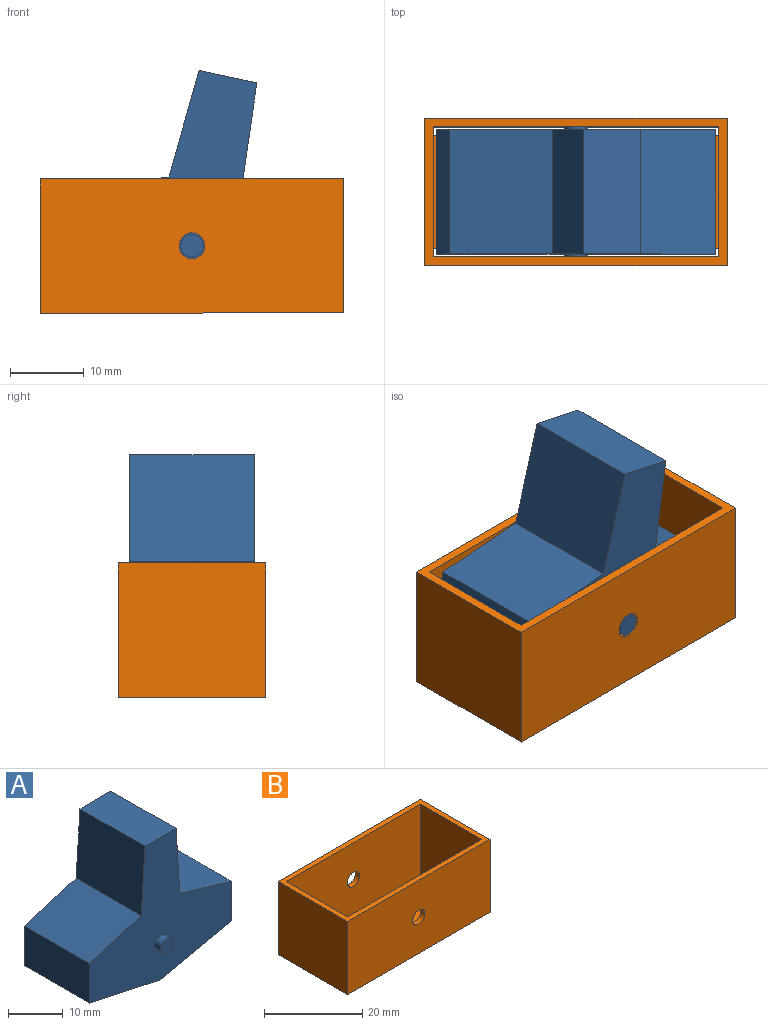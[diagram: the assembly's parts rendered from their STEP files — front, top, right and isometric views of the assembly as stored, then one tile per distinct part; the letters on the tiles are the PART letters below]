
ASSEMBLY  parts=2 mates=1
PART A: 15 faces, bbox 36.8x20x31.8 mm
  f0: plane 16.8x13.4mm, normal (0.29,0,0.96), area 234.9mm2, adj f1,f8,f9,f10
  f1: plane 16.8x15mm, normal (1,0,0.07), area 252.6mm2, adj f0,f2,f9,f10
  f2: plane 16.8x8mm, normal (0,0,1), area 134.4mm2, adj f1,f3,f9,f10
  f3: plane 16.8x15mm, normal (-1,0,0.07), area 252.6mm2, adj f2,f4,f9,f10
  f4: plane 16.8x13.4mm, normal (-0.29,0,0.96), area 234.9mm2, adj f3,f5,f9,f10
  f5: plane 16.8x8.8mm, normal (-1,0,0), area 147.8mm2, adj f4,f6,f9,f10
  f6: plane 18.4x16.8mm, normal (-0.21,0,-0.98), area 316.3mm2, adj f5,f7,f9,f10
  f7: plane 18.4x16.8mm, normal (0.21,0,-0.98), area 316.3mm2, adj f6,f8,f9,f10
  f8: plane 16.8x8.8mm, normal (1,0,0), area 147.8mm2, adj f0,f7,f9,f10
  f9: plane 36.8x31.8mm, normal (0,-1,0), area 619mm2, adj f0,f1,f2,f3,f4,f5,f6,f7
  f10: plane 36.8x31.8mm, normal (0,1,0), area 619mm2, adj f0,f1,f2,f3,f4,f5,f6,f7
  f11: plane 3x3mm, normal (0,1,0), area 7.1mm2, adj f12
  f12: cylinder r=1.5mm len=3mm, axis (0,1,0), area 15.1mm2, adj f10,f11
  f13: cylinder r=1.5mm len=3mm, axis (0,1,0), area 15.1mm2, adj f9,f14
  f14: plane 3x3mm, normal (0,-1,0), area 7.1mm2, adj f13
PART B: 15 faces, bbox 41x20x18.2 mm
  f0: plane 18.2x17.6mm, normal (-1,0,0), area 311.2mm2, adj f5,f6,f8,f9,f12,f13,f14
  f1: plane 41x18.2mm, normal (0,1,0), area 736.6mm2, adj f2,f7,f8,f9,f11
  f2: plane 20x18.2mm, normal (-1,0,0), area 364mm2, adj f1,f3,f8,f9
  f3: plane 41x18.2mm, normal (0,-1,0), area 736.6mm2, adj f2,f7,f8,f9,f10
  f4: plane 18.2x17.6mm, normal (1,0,0), area 311.2mm2, adj f5,f6,f8,f9,f12,f13,f14
  f5: plane 38.6x18.2mm, normal (0,-1,0), area 692.9mm2, adj f0,f4,f8,f9,f11
  f6: plane 38.6x18.2mm, normal (0,1,0), area 692.9mm2, adj f0,f4,f8,f9,f10
  f7: plane 20x18.2mm, normal (1,0,0), area 364mm2, adj f1,f3,f8,f9
  f8: plane 41x20mm, normal (0,0,1), area 140.6mm2, adj f0,f1,f2,f3,f4,f5,f6,f7
  f9: plane 41x20mm, normal (0,0,-1), area 727.4mm2, adj f0,f1,f2,f3,f4,f5,f6,f7
  f10: cylinder r=1.75mm len=3.5mm, axis (0,1,0), area 13.2mm2, adj f3,f6
  f11: cylinder r=1.75mm len=3.5mm, axis (0,1,0), area 13.2mm2, adj f1,f5
  f12: plane 38.6x0.6mm, normal (0,1,0), area 23.2mm2, adj f0,f4,f9,f14
  f13: plane 38.6x0.6mm, normal (0,-1,0), area 23.2mm2, adj f0,f4,f9,f14
  f14: plane 38.6x15.2mm, normal (0,0,1), area 586.7mm2, adj f0,f4,f12,f13
PLACE A rot(axis=(0,1,0),12deg) t=(-20.27,8.9,-30.84)mm
PLACE B rot(axis=(0,-1,0),0.2deg) t=(-9.63,-2.69,-45.19)mm
MATE revolute B.f10 <-> A.f12  axis (0,-1,0) through (-13.75,-9.5,-36.11)mm
